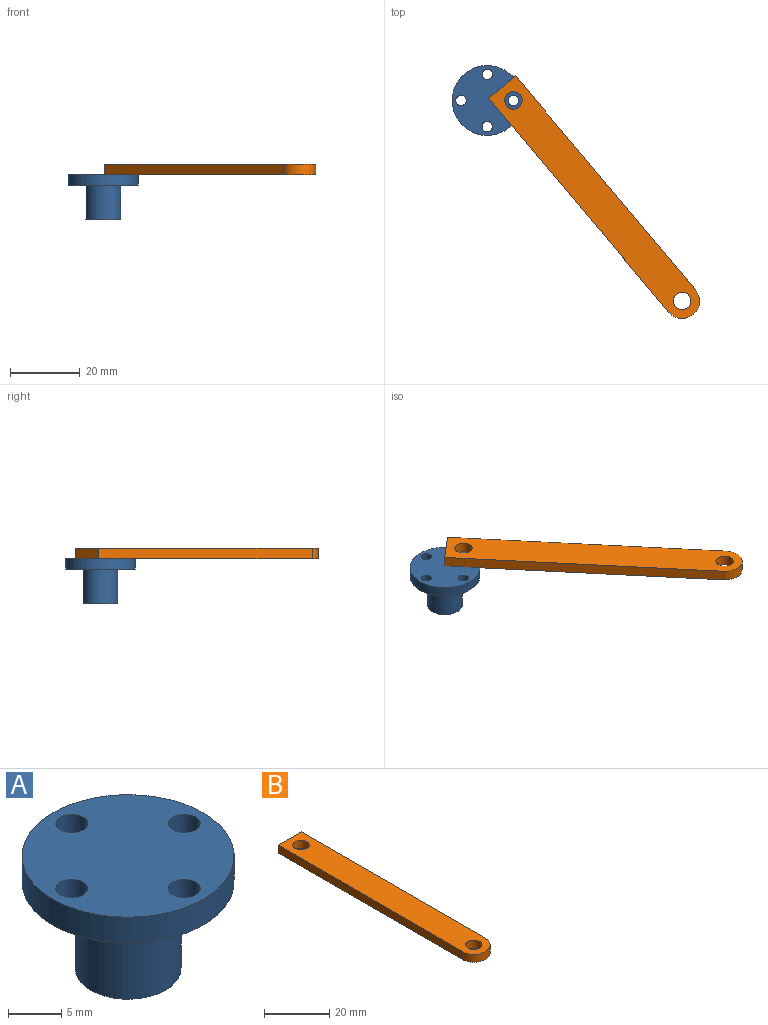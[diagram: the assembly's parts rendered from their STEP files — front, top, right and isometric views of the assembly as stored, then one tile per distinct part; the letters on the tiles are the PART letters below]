
ASSEMBLY  parts=2 mates=1
PART A: 13 faces, bbox 20x20x13 mm
  f0: cylinder r=5mm len=10mm, axis (0,0,-1), area 309.2mm2, adj f3,f4,f5
  f1: cylinder r=2.5mm len=10mm, axis (0,0,-1), area 110.7mm2, adj f2,f3,f12
  f2: plane 10x4mm, normal (-1,0,0), area 35.1mm2, adj f1,f3,f4,f12
  f3: plane 10x10mm, normal (0,0,-1), area 61.7mm2, adj f0,f1,f2
  f4: cylinder r=1.25mm len=3.5mm, axis (-1,0,0), area 26.9mm2, adj f0,f2
  f5: plane 20x20mm, normal (0,0,-1), area 207.3mm2, adj f0,f7,f8,f9,f10,f11
  f6: plane 20x20mm, normal (0,0,1), area 285.9mm2, adj f7,f8,f9,f10,f11
  f7: cylinder r=10mm len=20mm, axis (0,0,-1), area 188.5mm2, adj f5,f6
  f8: cylinder r=1.5mm len=3mm, axis (0,0,-1), area 28.3mm2, adj f5,f6
  f9: cylinder r=1.5mm len=3mm, axis (0,0,-1), area 28.3mm2, adj f5,f6
  f10: cylinder r=1.5mm len=3mm, axis (0,0,-1), area 28.3mm2, adj f5,f6
  f11: cylinder r=1.5mm len=3mm, axis (0,0,-1), area 28.3mm2, adj f5,f6
  f12: plane 5x4mm, normal (0,0,-1), area 16.8mm2, adj f1,f2
PART B: 8 faces, bbox 10x85x3 mm
  f0: cylinder r=5mm len=10mm, axis (0,0,-1), area 47.1mm2, adj f1,f4,f6,f7
  f1: plane 80x3mm, normal (1,0,0), area 240mm2, adj f0,f2,f6,f7
  f2: plane 10x3mm, normal (0,1,0), area 30mm2, adj f1,f4,f6,f7
  f3: cylinder r=2.5mm len=5mm, axis (0,0,-1), area 47.1mm2, adj f6,f7
  f4: plane 80x3mm, normal (-1,0,0), area 240mm2, adj f0,f2,f6,f7
  f5: cylinder r=2.5mm len=5mm, axis (0,0,-1), area 47.1mm2, adj f6,f7
  f6: plane 85x10mm, normal (0,0,1), area 800mm2, adj f0,f1,f2,f3,f4,f5
  f7: plane 85x10mm, normal (0,0,-1), area 800mm2, adj f0,f1,f2,f3,f4,f5
PLACE A t=(-0.12,22.9,-24.14)mm fixed
PLACE B rot(axis=(0,0,1),40.1deg) t=(29.92,-3.88,-11.14)mm
MATE revolute A.f8 <-> B.f5  axis (0,0,-1) through (7.38,22.9,-11.14)mm
